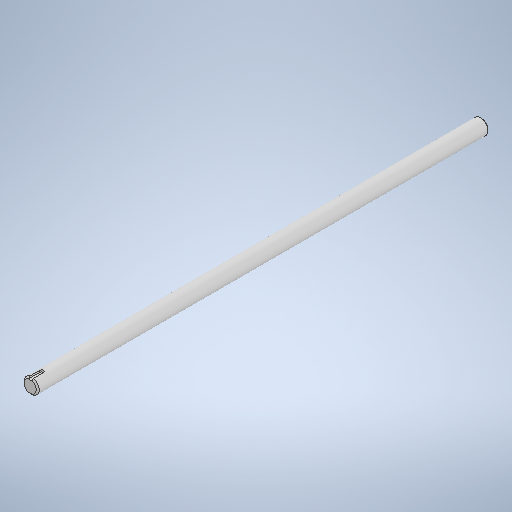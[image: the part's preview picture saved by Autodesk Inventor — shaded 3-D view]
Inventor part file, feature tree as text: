
AUTODESK INVENTOR PART (.ipt)
format: ipt  version: 2025.1 (Build 291241000, 241)  size: 269,312 bytes
history: native  units: in
note: dims shown in document units (in); Inventor stores cm internally (conversion verified against a paired STEP export)
features: extrude x2, sketch x2, chamfer x1, plane x1
ambient origin geometry x8: Origin, YZ Plane, XZ Plane, XY Plane, X Axis, Y Axis, Z Axis, Center Point
bodies: Solid1 (feature_tree)
feature tree (6):
  chamfer  "Chamfer1"  Distance=0.0625in
  plane  "Work Plane1"
  extrude  "Extrusion1"  Depth=0.0625in TaperAngle=0.0deg
  extrude  "Extrusion2"  [1 undecoded]
  sketch  "Sketch2"  dims[d0=0.125in]
  sketch  "Sketch3"  dims[d1=0.375in d2=0.0625in d3=0.0in d4=0.0625in d5=0.0in]
note: 1 required parameter value undecoded (feature->parameter linkage not recoverable at this tier; creation-order binding heuristic only, values carry confidence <= 0.55)
